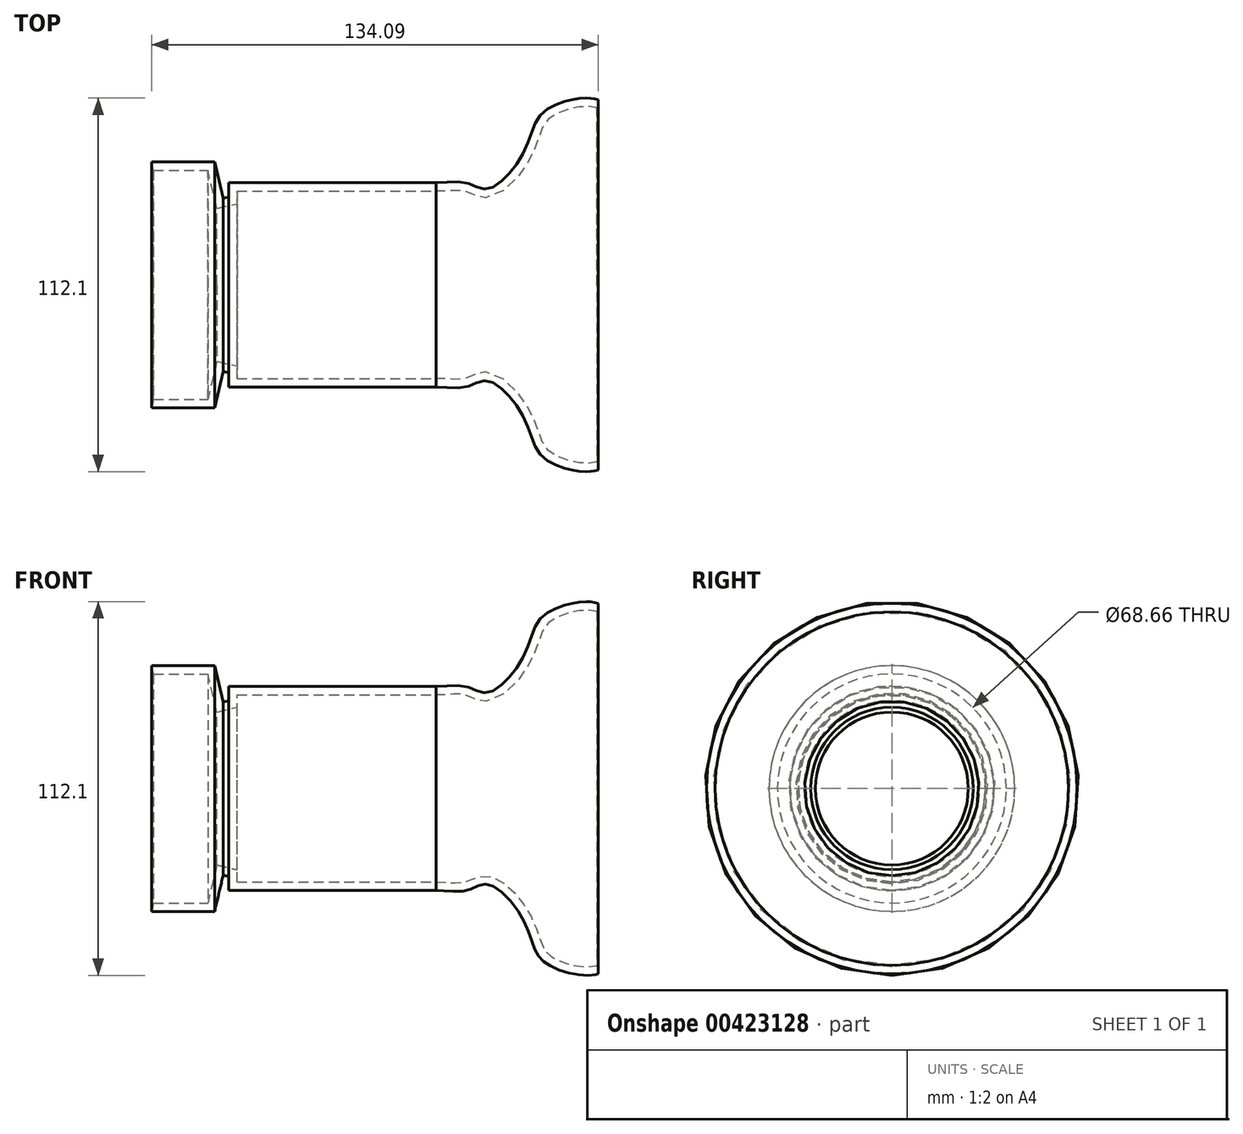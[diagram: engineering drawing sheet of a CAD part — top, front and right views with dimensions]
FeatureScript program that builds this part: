
annotation { "Feature Type Name" : "Feature", "Feature Type Description" : "" }
export const myFeature = defineFeature(function(context is Context, id is Id, definition is map)
    precondition{}
    {
        {
            var Q0;
            Q0=qCreatedBy(makeId("Front.planeOp"),FACE);
            var sketch = newSketch(context, id + "F0", { "sketchPlane" : qUnion([Q0])});
            skLineSegment(sketch, "E0", {"start": v(-34.94, 30.63) * mm, "end": v(27.35, 30.63) * mm});
            skFitSpline(sketch, "E1", {"points": [v(27.35, 30.63) * mm, v(36.27, 30.63) * mm, v(42.67, 28.74) * mm, v(52.91, 38.37) * mm, v(57.26, 48.83) * mm, v(62.07, 53.49) * mm, v(72.7, 56.04) * mm, v(76.04, 55.6) * mm], "startDerivative": vector(40.66, -3.7) * mm, "endDerivative": vector(4.9, -0.84) * mm});
            skLineSegment(sketch, "E2", {"start": v(76.04, 55.6) * mm, "end": v(76.04, 0) * mm});
            skLineSegment(sketch, "E3", {"start": v(76.04, 0) * mm, "end": v(-49.31, 0) * mm});
            skLineSegment(sketch, "E4", {"start": v(-49.31, 0) * mm, "end": v(-58.05, 36.87) * mm});
            skLineSegment(sketch, "E5", {"start": v(-58.05, 36.87) * mm, "end": v(-39.12, 36.87) * mm});
            skLineSegment(sketch, "E6", {"start": v(-39.12, 36.87) * mm, "end": v(-36.54, 26) * mm});
            skLineSegment(sketch, "E7", {"start": v(-36.54, 26) * mm, "end": v(-34.94, 26.38) * mm});
            skLineSegment(sketch, "E8", {"start": v(-34.94, 26.38) * mm, "end": v(-34.94, 30.63) * mm});
            skPoint(sketch, "E9.orphan", {"position": v(-56.57, 30.63) * mm});
            skSolve(sketch);
        }
        {
            var Q0;
            Q0=makeQuery(id+"F0.imprint","IMPRINT",FACE,{"disambiguationData":[TD([[makeQuery(id+"F0.imprint","IMPRINT",EDGE,{"derivedFrom":sQuery(id+"F0.wireOp",EDGE,"E0")}),-1.0]])]});
            var Q1;
            Q1=sQuery(id+"F0.wireOp",EDGE,"E3");
            revolve(context, id + "F1", {"entities" : qUnion([Q0]), "axis" : qUnion([Q1]), "revolveType" : RevolveType.FULL});
        }
        {
            var Q0;
            Q0=makeQuery(id+"F1.opRevolve","SWEPT_FACE",FACE,{"disambiguationData":[OSD([sQuery(id+"F0.wireOp",EDGE,"E4")])]});
            var Q1;
            Q1=makeQuery(id+"F1.opRevolve","SWEPT_FACE",FACE,{"disambiguationData":[OSD([sQuery(id+"F0.wireOp",EDGE,"E2")])]});
            var Q2;
            Q2=makeQuery(id+"F1.opRevolve","SWEPT_BODY",BODY,{"disambiguationData":[OSD([sQuery(id+"F0.wireOp",EDGE,"E0"),sQuery(id+"F0.wireOp",EDGE,"E1"),sQuery(id+"F0.wireOp",EDGE,"E2"),sQuery(id+"F0.wireOp",EDGE,"E3"),sQuery(id+"F0.wireOp",EDGE,"E4"),sQuery(id+"F0.wireOp",EDGE,"E5"),sQuery(id+"F0.wireOp",EDGE,"E6"),sQuery(id+"F0.wireOp",EDGE,"E7"),sQuery(id+"F0.wireOp",EDGE,"E8")])]});
            shell(context, id + "F2", {"entities" : qUnion([Q0, Q1]), "parts" : qUnion([Q2]), "thickness" : 2.54 * mm});
        }
    });
